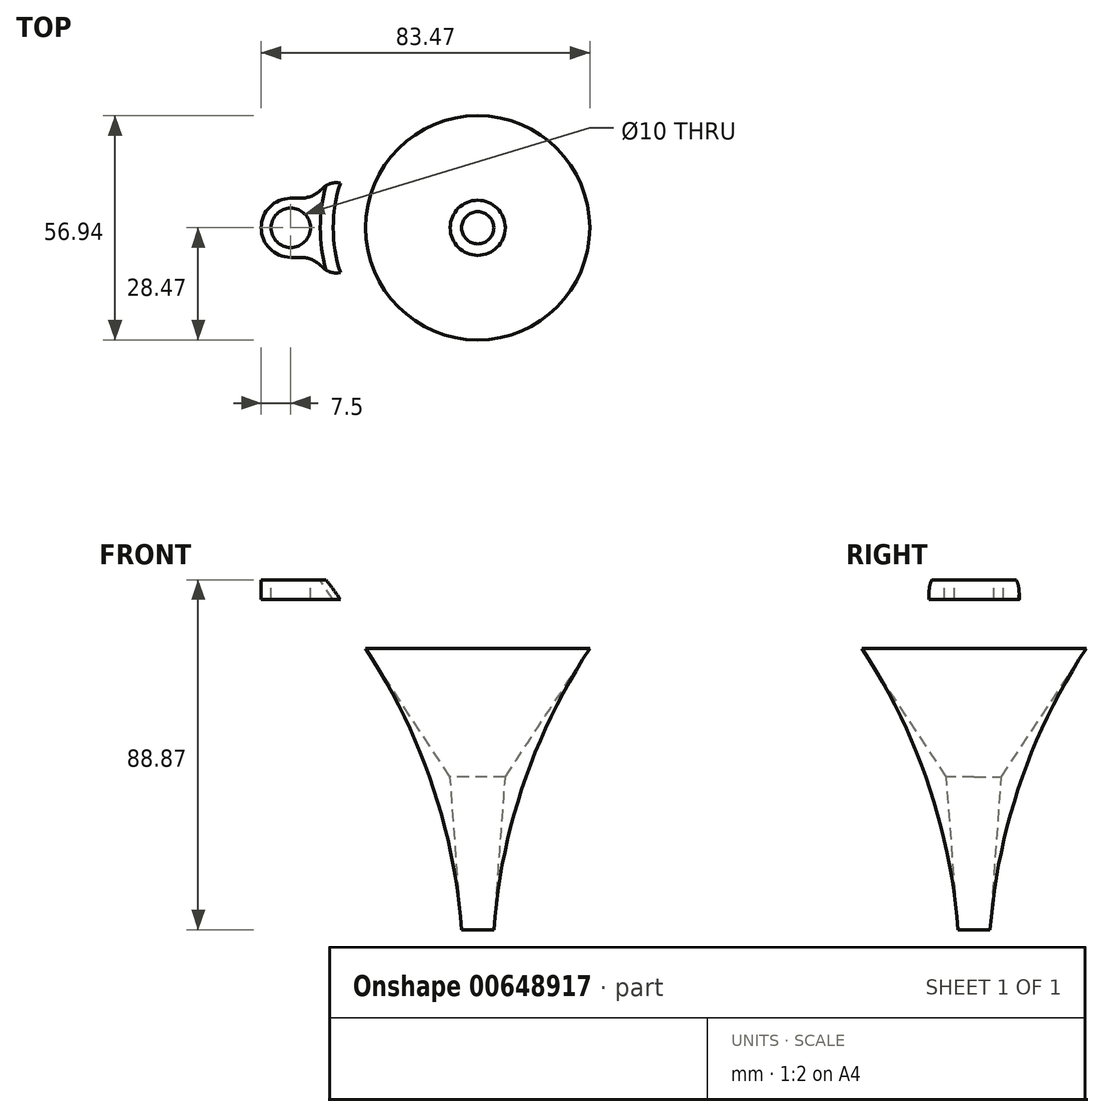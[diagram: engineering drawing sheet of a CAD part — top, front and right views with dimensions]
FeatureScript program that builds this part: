
annotation { "Feature Type Name" : "Feature", "Feature Type Description" : "" }
export const myFeature = defineFeature(function(context is Context, id is Id, definition is map)
    precondition{}
    {
        {
            var Q0;
            Q0=qCreatedBy(makeId("Front.planeOp"),FACE);
            var sketch = newSketch(context, id + "F0", { "sketchPlane" : qUnion([Q0])});
            skLineSegment(sketch, "E0", {"start": v(-4, 0) * mm, "end": v(-7, 40) * mm});
            skLineSegment(sketch, "E1", {"start": v(-7, 40) * mm, "end": v(-40, 90) * mm});
            skLineSegment(sketch, "E2", {"start": v(-4, 0) * mm, "end": v(0, 0) * mm});
            skLineSegment(sketch, "E3", {"start": v(-40, 90) * mm, "end": v(0, 90) * mm});
            skLineSegment(sketch, "E4", {"start": v(0, 90) * mm, "end": v(0, 0) * mm});
            skSolve(sketch);
        }
        {
            var Q0;
            Q0=makeQuery(id+"F0.imprint","IMPRINT",FACE,{"disambiguationData":[TD([[makeQuery(id+"F0.imprint","IMPRINT",EDGE,{"derivedFrom":sQuery(id+"F0.wireOp",EDGE,"E0")}),-1.0]])]});
            var Q1;
            Q1=sQuery(id+"F0.wireOp",EDGE,"E4");
            revolve(context, id + "F1", {"entities" : qUnion([Q0]), "axis" : qUnion([Q1]), "revolveType" : RevolveType.FULL});
        }
        {
            var Q0;
            Q0=makeQuery(id+"F1.opRevolve","SWEPT_EDGE",EDGE,{"disambiguationData":[OSD([sQuery(id+"F0.wireOp",EDGE,"E0"),sQuery(id+"F0.wireOp",EDGE,"E1")])]});
            fillet(context, id + "F2", {"entities" : qUnion([Q0]), "radius" : 150 * mm, "tangentPropagation" : true, "allowEdgeOverflow" : false});
        }
        {
            var Q0;
            Q0=makeQuery(id+"F1.opRevolve","SWEPT_FACE",FACE,{"disambiguationData":[OSD([sQuery(id+"F0.wireOp",EDGE,"E3")])]});
            var sketch = newSketch(context, id + "F3", { "sketchPlane" : qUnion([Q0])});
            skLineSegment(sketch, "E5.bottom", {"start": v(-47.5, 7.5) * mm, "end": v(-45.07, 7.5) * mm});
            skLineSegment(sketch, "E5.top", {"start": v(-47.5, -7.5) * mm, "end": v(-45.07, -7.5) * mm});
            skLineSegment(sketch, "E5.left", {"start": v(-55, 0) * mm, "end": v(-55, 0) * mm});
            skLineSegment(sketch, "E5.right", {"start": v(-25, 7.5) * mm, "end": v(-25, -7.5) * mm, "construction": true});
            skPoint(sketch, "E5.middle", {"position": v(-40, 0) * mm});
            skCircle(sketch, "E6", {"center": v(-47.5, 0) * mm, "radius": 5 * mm});
            skArc(sketch, "E7", {"start": v(-39.3, 7.5) * mm, "mid": v(-40, 0) * mm, "end": v(-39.3, -7.5) * mm});
            skArc(sketch, "E8", {"start": v(-37.95, -12.63) * mm, "mid": v(40, 0) * mm, "end": v(-37.95, 12.63) * mm, "construction": true});
            skLineSegment(sketch, "E9", {"start": v(-39.3, 7.5) * mm, "end": v(-25, 7.5) * mm, "construction": true});
            skLineSegment(sketch, "E10", {"start": v(-39.3, -7.5) * mm, "end": v(-25, -7.5) * mm, "construction": true});
            skPoint(sketch, "E11.visualSharp", {"position": v(-39.3, 7.5) * mm});
            skArc(sketch, "E11.filletArc", {"start": v(-45.07, 7.5) * mm, "mid": v(-40.68, 8.92) * mm, "end": v(-37.95, 12.63) * mm});
            skPoint(sketch, "E12.visualSharp", {"position": v(-39.3, -7.5) * mm});
            skArc(sketch, "E12.filletArc", {"start": v(-37.95, -12.63) * mm, "mid": v(-40.68, -8.92) * mm, "end": v(-45.07, -7.5) * mm});
            skPoint(sketch, "E13.visualSharp", {"position": v(-55, -7.5) * mm});
            skArc(sketch, "E13.filletArc", {"start": v(-55, 0) * mm, "mid": v(-52.8, -5.3) * mm, "end": v(-47.5, -7.5) * mm});
            skPoint(sketch, "E14.visualSharp", {"position": v(-55, 7.5) * mm});
            skArc(sketch, "E14.filletArc", {"start": v(-47.5, 7.5) * mm, "mid": v(-52.8, 5.3) * mm, "end": v(-55, 0) * mm});
            skLineSegment(sketch, "E15", {"start": v(-37.95, -12.63) * mm, "end": v(-25, -7.5) * mm});
            skLineSegment(sketch, "E16", {"start": v(-37.95, 12.63) * mm, "end": v(-25, 7.5) * mm});
            skLineSegment(sketch, "E17", {"start": v(-25, -7.5) * mm, "end": v(-25, 7.5) * mm});
            skSolve(sketch);
        }
        {
            var Q0;
            Q0=makeQuery(id+"F3.imprint","IMPRINT",FACE,{"disambiguationData":[TD([[makeQuery(id+"F3.imprint","IMPRINT",EDGE,{"derivedFrom":sQuery(id+"F3.wireOp",EDGE,"E5.bottom")}),-1.0]])]});
            var Q1;
            {var subQ2=sQuery(id+"F3.wireOp",EDGE,"E7");Q1=makeQuery(id+"F3.imprint","IMPRINT",FACE,{"disambiguationData":[TD([[makeQuery(id+"F3.imprint","IMPRINT",EDGE,{"derivedFrom":subQ2}),1.0]])]});}
            extrude(context, id + "F4", {"entities" : qUnion([Q0, Q1]), "oppositeDirection" : true, "depth" : 5 * mm, "offsetDistance" : 25 * mm});
        }
        {
            var Q0;
            Q0 = qSketchRegion(id + "F0", true);
            var Q1;
            Q1=sQuery(id+"F0.wireOp",EDGE,"E4");
            revolve(context, id + "F5", {"operationType" : NewBodyOperationType.REMOVE, "entities" : qUnion([Q0]), "axis" : qUnion([Q1]), "revolveType" : RevolveType.FULL, "oppositeDirection" : true});
        }
        {
            var Q0;
            Q0=makeQuery(id+"F4.opExtrude","SWEPT_EDGE",EDGE,{"disambiguationData":[OSD([sQuery(id+"F0.wireOp",EDGE,"E1"),sQuery(id+"F0.wireOp",EDGE,"E3"),sQuery(id+"F3.wireOp",EDGE,"E12.filletArc"),sQuery(id+"F3.wireOp",EDGE,"E15")])]});
            var Q1;
            Q1=makeQuery(id+"F4.opExtrude","SWEPT_EDGE",EDGE,{"disambiguationData":[OSD([sQuery(id+"F0.wireOp",EDGE,"E1"),sQuery(id+"F0.wireOp",EDGE,"E3"),sQuery(id+"F3.wireOp",EDGE,"E11.filletArc"),sQuery(id+"F3.wireOp",EDGE,"E16")])]});
            fillet(context, id + "F6", {"entities" : qUnion([Q0, Q1]), "radius" : 5 * mm, "tangentPropagation" : true, "allowEdgeOverflow" : false});
        }
    });
